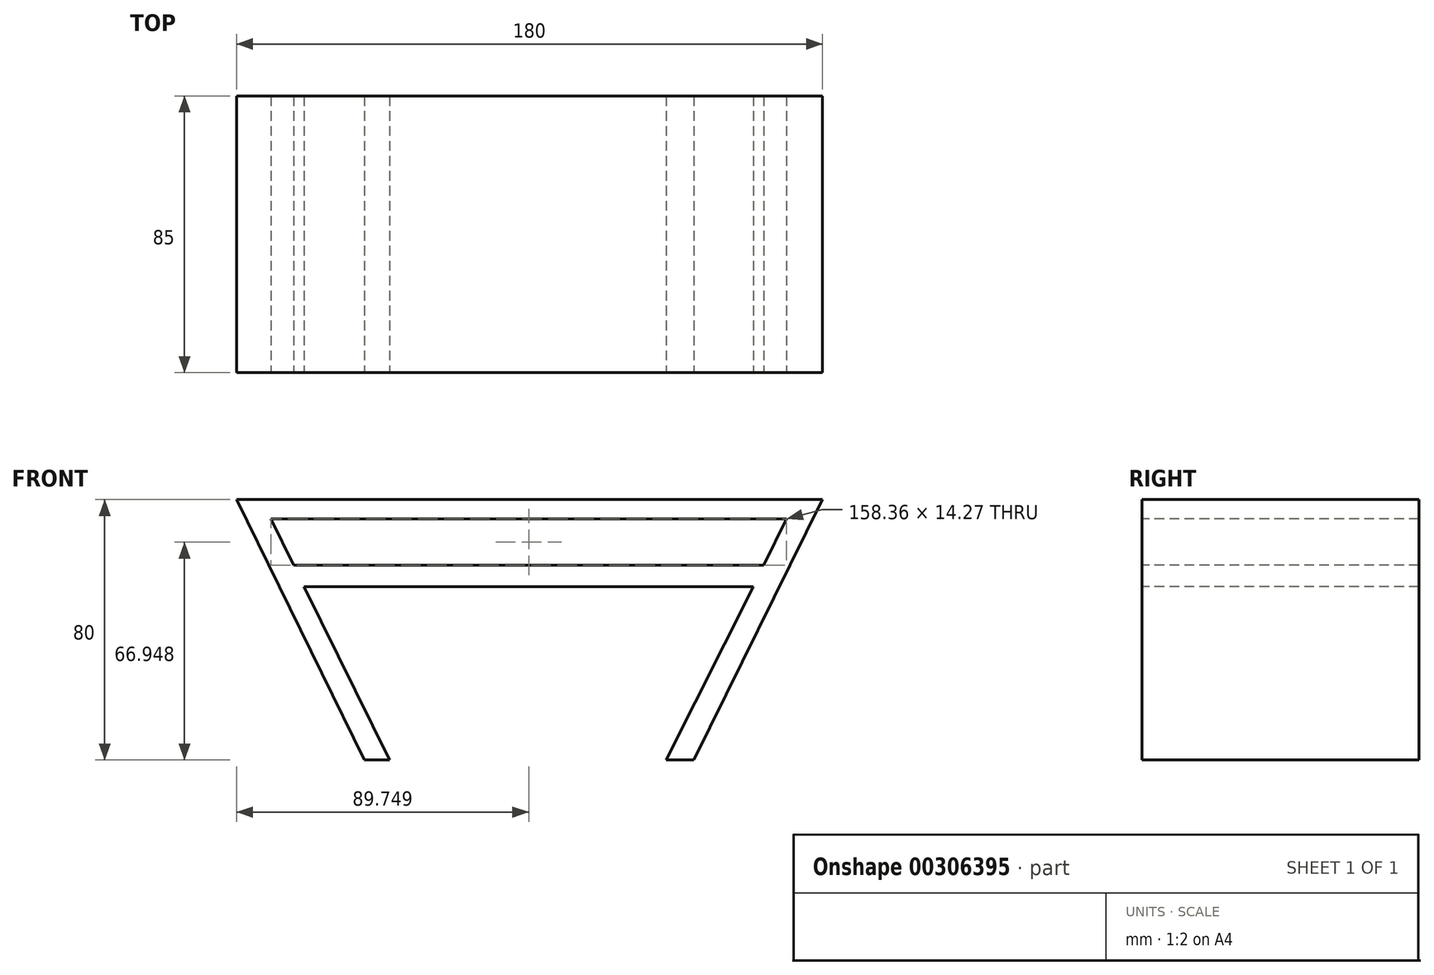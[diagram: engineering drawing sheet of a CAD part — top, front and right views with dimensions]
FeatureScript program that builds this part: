
annotation { "Feature Type Name" : "Feature", "Feature Type Description" : "" }
export const myFeature = defineFeature(function(context is Context, id is Id, definition is map)
    precondition{}
    {
        {
            var Q0;
            Q0=qCreatedBy(makeId("Front.planeOp"),FACE);
            var sketch = newSketch(context, id + "F0", { "sketchPlane" : qUnion([Q0])});
            skLineSegment(sketch, "E0.bottom", {"start": v(-85.28, 51.99) * mm, "end": v(94.72, 51.99) * mm});
            skLineSegment(sketch, "E0.top", {"start": v(-85.28, -28.01) * mm, "end": v(94.72, -28.01) * mm});
            skLineSegment(sketch, "E0.left", {"start": v(-85.28, 51.99) * mm, "end": v(-85.28, -28.01) * mm});
            skLineSegment(sketch, "E0.right", {"start": v(94.72, 51.99) * mm, "end": v(94.72, -28.01) * mm});
            skSolve(sketch);
        }
        {
            var Q0;
            Q0=makeQuery(id+"F0.imprint","IMPRINT",FACE,{"disambiguationData":[TD([[makeQuery(id+"F0.imprint","IMPRINT",EDGE,{"derivedFrom":sQuery(id+"F0.wireOp",EDGE,"E0.bottom")}),-1.0]])]});
            extrude(context, id + "F1", {"entities" : qUnion([Q0]), "depth" : 85 * mm});
        }
        {
            var Q0;
            Q0=makeQuery(id+"F1.opExtrude","CAP_FACE",FACE,{"disambiguationData":[OSD([sQuery(id+"F0.wireOp",EDGE,"E0.bottom"),sQuery(id+"F0.wireOp",EDGE,"E0.top"),sQuery(id+"F0.wireOp",EDGE,"E0.left"),sQuery(id+"F0.wireOp",EDGE,"E0.right")])],"isStart":false});
            var sketch = newSketch(context, id + "F2", { "sketchPlane" : qUnion([Q0])});
            skLineSegment(sketch, "E1", {"start": v(-85.28, 51.99) * mm, "end": v(-46, -28.01) * mm});
            skLineSegment(sketch, "E2", {"start": v(94.72, 51.99) * mm, "end": v(55.23, -28.01) * mm});
            skSolve(sketch);
        }
        {
            var Q0;
            Q0 = qSketchRegion(id + "F2", true);
            var Q1;
            {var subQ0=sQuery(id+"F2.wireOp",EDGE,"E1");Q1=makeQuery(id+"F2.imprint","IMPRINT",FACE,{"disambiguationData":[TD([[makeQuery(id+"F2.imprint","IMPRINT",EDGE,{"derivedFrom":subQ0}),-1.0]])]});}
            var Q2;
            {var subQ0=sQuery(id+"F2.wireOp",EDGE,"E2");Q2=makeQuery(id+"F2.imprint","IMPRINT",FACE,{"disambiguationData":[TD([[makeQuery(id+"F2.imprint","IMPRINT",EDGE,{"derivedFrom":subQ0}),1.0]])]});}
            extrude(context, id + "F3", {"entities" : qUnion([Q0, Q1, Q2]), "operationType" : NewBodyOperationType.REMOVE, "endBound" : BoundingType.THROUGH_ALL, "oppositeDirection" : true, "depth" : 25 * mm});
        }
        {
            var Q0;
            Q0=makeQuery(id+"F1.opExtrude","CAP_FACE",FACE,{"disambiguationData":[OSD([sQuery(id+"F0.wireOp",EDGE,"E0.bottom"),sQuery(id+"F0.wireOp",EDGE,"E0.top"),sQuery(id+"F0.wireOp",EDGE,"E0.left"),sQuery(id+"F0.wireOp",EDGE,"E0.right")])],"isStart":false});
            var sketch = newSketch(context, id + "F4", { "sketchPlane" : qUnion([Q0])});
            skLineSegment(sketch, "E3", {"start": v(-75.37, 31.8) * mm, "end": v(84.76, 31.8) * mm});
            skLineSegment(sketch, "E4", {"start": v(-72.17, 25.3) * mm, "end": v(81.54, 25.3) * mm});
            skLineSegment(sketch, "E5", {"start": v(-77.61, 51.99) * mm, "end": v(-67.7, 31.8) * mm});
            skLineSegment(sketch, "E6", {"start": v(-67.7, 31.8) * mm, "end": v(-38.34, -28.01) * mm});
            skLineSegment(sketch, "E7", {"start": v(86.53, 51.99) * mm, "end": v(76.7, 31.8) * mm});
            skLineSegment(sketch, "E8", {"start": v(76.7, 31.8) * mm, "end": v(46.69, -28.01) * mm});
            skLineSegment(sketch, "E9", {"start": v(-74.7, 46.07) * mm, "end": v(83.65, 46.07) * mm});
            skSolve(sketch);
        }
        {
            var Q0;
            {var subQ5=sQuery(id+"F4.wireOp",EDGE,"E9");Q0=makeQuery(id+"F4.imprint","IMPRINT",FACE,{"disambiguationData":[TD([[makeQuery(id+"F4.imprint","IMPRINT",EDGE,{"derivedFrom":subQ5}),-1.0]])]});}
            var Q1;
            {var subQ0=sQuery(id+"F4.wireOp",EDGE,"E6");var subQ1=sQuery(id+"F4.wireOp",EDGE,"E4");var subQ2=makeQuery(id+"F4.imprint","INTERSECT",VERTEX,{"derivedFrom":[subQ1,subQ0]});Q1=makeQuery(id+"F4.imprint","IMPRINT",FACE,{"disambiguationData":[TD([[makeQuery(id+"F4.imprint","IMPRINT",EDGE,{"disambiguationData":[TD([[subQ2,-1.0]])],"derivedFrom":subQ1}),-1.0]])]});}
            extrude(context, id + "F5", {"entities" : qUnion([Q0, Q1]), "operationType" : NewBodyOperationType.REMOVE, "endBound" : BoundingType.THROUGH_ALL, "oppositeDirection" : true, "depth" : 25 * mm});
        }
    });
